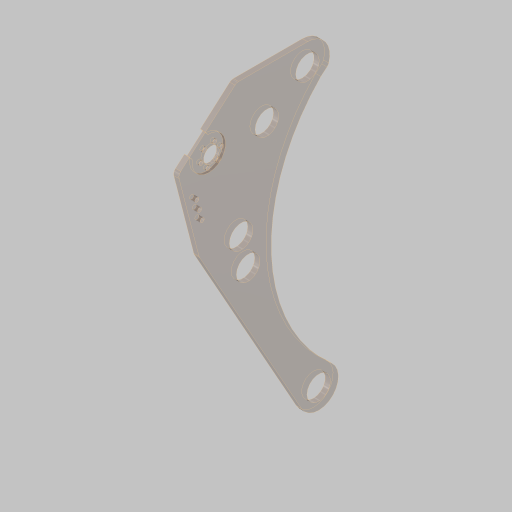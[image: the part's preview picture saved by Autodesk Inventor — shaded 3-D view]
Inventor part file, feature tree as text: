
AUTODESK INVENTOR PART (.ipt)
format: ipt  version: 2023.5 (Build 275446000, 446)  size: 281,600 bytes
history: native  units: in
note: dims shown in document units (in); Inventor stores cm internally (conversion verified against a paired STEP export)
features: sketch x8, projected_geometry x6, extrude x5, hole x2, fillet x1
ambient origin geometry x8: Origin, YZ Plane, XZ Plane, XY Plane, X Axis, Y Axis, Z Axis, Center Point
bodies: Body1 (feature_tree)
feature tree (22):
  sketch  "Sketch1"  dims[d0=16.0in d1=3.0in]
  extrude  "Extrusion2"  Depth=3.0in
  hole  "Hole2"  [1 undecoded]
  extrude  "Extrusion3"  Depth=7.0in
  fillet  "Fillet1"  Radius=1.125in
  extrude  "Extrusion4"  Depth=0.375in
  extrude  "Extrusion6"  Depth=3.75in
  hole  "Hole5"  [1 undecoded]
  extrude  "Extrusion7"  Depth=1.0in
  sketch  "Sketch4"  dims[d2=0.25in d4=4.5in]
  sketch  "Sketch5"  dims[d5=11.875in d6=7.0in d27=1.125in]
  sketch  "Sketch6"  dims[d29=0.375in d31=4.0in]
  projected_geometry  "Projected Loop1"
  sketch  "Sketch8"  dims[d33=4.0in d35=3.75in]
  sketch  "Sketch11"  dims[d36=0.25in d37=0.0in d39=0.5in]
  sketch  "Sketch12"  dims[d41=0.201in d42=0.75in d43=0.385in d44=0.25in d45=0.5635in d46=1.0in d47=0.8108in d51=6.5in]
  sketch  "Sketch13"  dims[d52=11.0in d53=1.2075in d57=1.0in d58=11.75in d59=12.75in d60=1.25in d63=1.0in d64=0.0in d65=0.5in d66=0.26in d76=0.602in d77=1.5in d78=2.256in d79=4.7708in d81=1.0in d83=0.75in d84=1.125in d85=6.2598in d87=1.5in d88=7.4409in d90=1.0in d91=0.0in d111=1.25in d112=1.6in d113=1.0in d114=0.125in d115=0.0in d116=1.0in d117=0.75in d118=2.3622in d120=360.0deg d122=0.201in d123=0.75in d124=0.385in d125=0.25in d126=0.5635in d127=1.0in d128=0.8108in d129=2.256in d130=2.6463in d133=1.125in d134=1.87in d135=2.815in d136=0.125in d137=0.0in]
  projected_geometry  "Project Cut Edges1"
  projected_geometry  "Project Cut Edges4"
  projected_geometry  "Project Cut Edges5"
  projected_geometry  "Project Cut Edges6"
  projected_geometry  "Project Cut Edges7"
note: 2 required parameter values undecoded (feature->parameter linkage not recoverable at this tier; creation-order binding heuristic only, values carry confidence <= 0.55)
